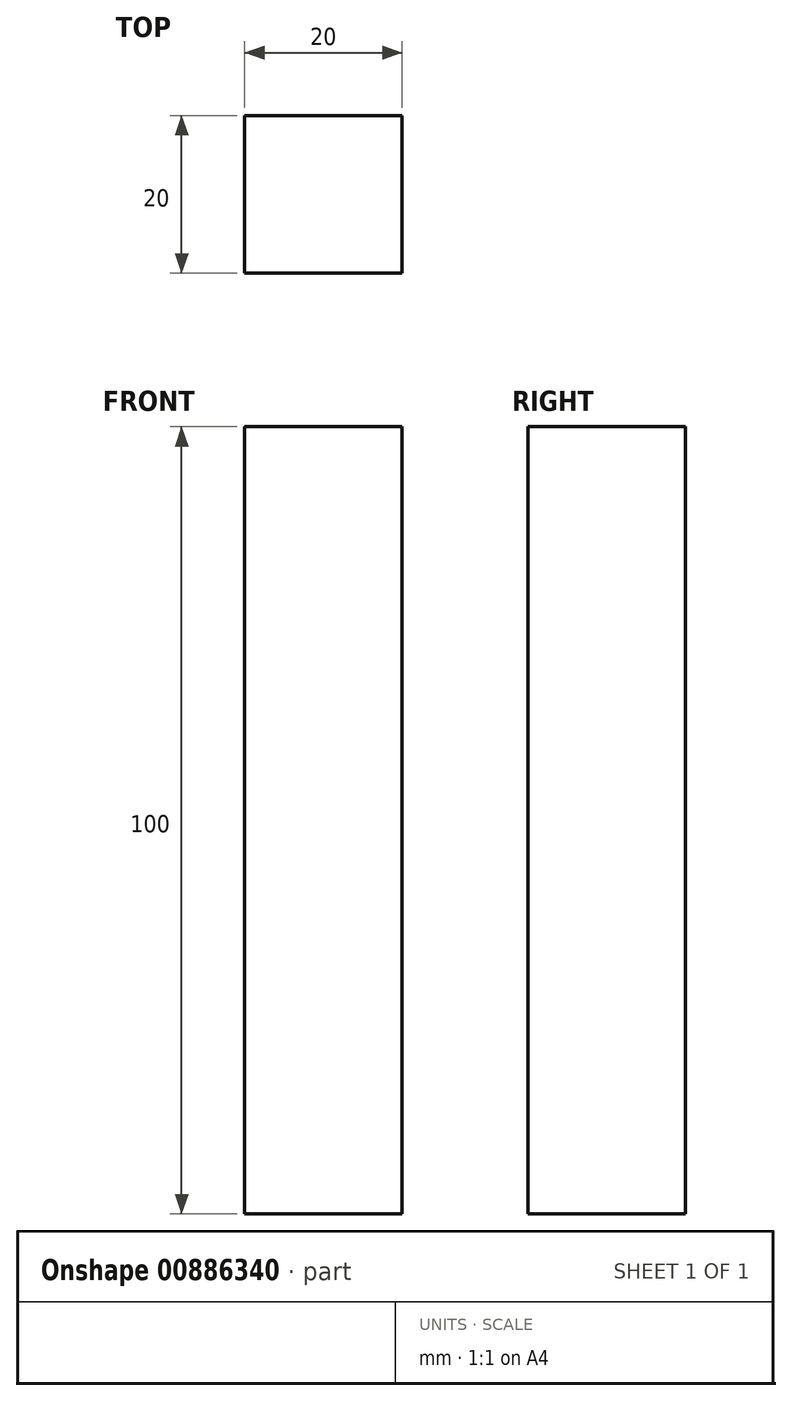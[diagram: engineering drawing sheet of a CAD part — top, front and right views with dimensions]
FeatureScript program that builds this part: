
annotation { "Feature Type Name" : "Feature", "Feature Type Description" : "" }
export const myFeature = defineFeature(function(context is Context, id is Id, definition is map)
    precondition{}
    {
        {
            var Q0;
            Q0=qCreatedBy(makeId("Top.planeOp"),FACE);
            var sketch = newSketch(context, id + "F0", { "sketchPlane" : qUnion([Q0])});
            skLineSegment(sketch, "E0.bottom", {"start": v(10, 10) * mm, "end": v(-10, 10) * mm});
            skLineSegment(sketch, "E0.top", {"start": v(10, -10) * mm, "end": v(-10, -10) * mm});
            skLineSegment(sketch, "E0.left", {"start": v(10, 10) * mm, "end": v(10, -10) * mm});
            skLineSegment(sketch, "E0.right", {"start": v(-10, 10) * mm, "end": v(-10, -10) * mm});
            skPoint(sketch, "E0.middle", {"position": v(0, 0) * mm});
            skSolve(sketch);
        }
        {
            var Q0;
            Q0 = qSketchRegion(id + "F0", true);
            extrude(context, id + "F1", {"entities" : qUnion([Q0]), "depth" : 100 * mm, "offsetDistance" : 25 * mm});
        }
    });
